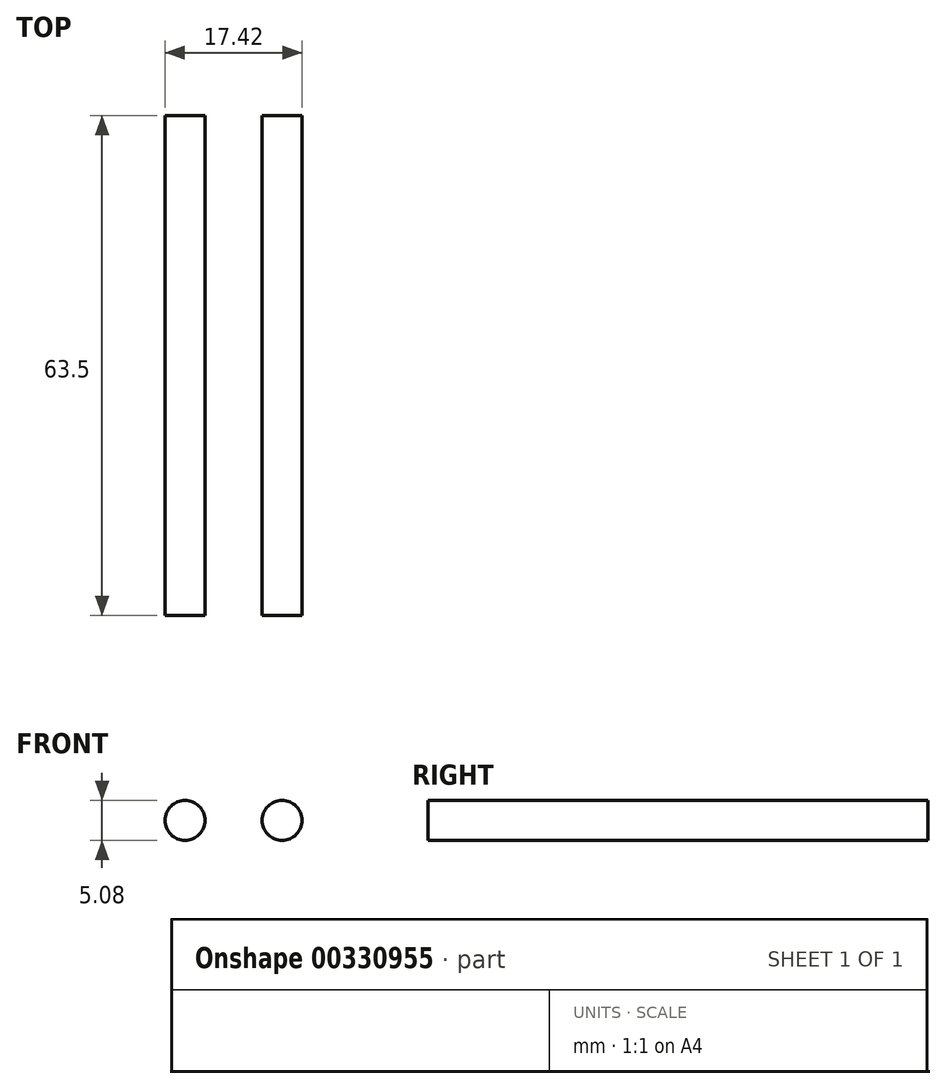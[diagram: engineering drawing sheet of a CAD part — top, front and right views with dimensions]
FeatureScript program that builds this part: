
annotation { "Feature Type Name" : "Feature", "Feature Type Description" : "" }
export const myFeature = defineFeature(function(context is Context, id is Id, definition is map)
    precondition{}
    {
        {
            var Q0;
            Q0=qCreatedBy(makeId("Front.planeOp"),FACE);
            var sketch = newSketch(context, id + "F0", { "sketchPlane" : qUnion([Q0])});
            skLineSegment(sketch, "E0", {"start": v(-3.56, 30.72) * mm, "end": v(-30.55, -10.44) * mm});
            skLineSegment(sketch, "E1", {"start": v(-25.24, -20.27) * mm, "end": v(0, -20.27) * mm});
            skLineSegment(sketch, "E2.MirrorCS", {"start": v(3.56, 30.72) * mm, "end": v(30.55, -10.44) * mm});
            skLineSegment(sketch, "E3.MirrorCS", {"start": v(25.24, -20.27) * mm, "end": v(0, -20.27) * mm});
            skPoint(sketch, "E4.visualSharp", {"position": v(-37, -20.27) * mm});
            skArc(sketch, "E4.filletArc", {"start": v(-30.55, -10.44) * mm, "mid": v(-30.83, -16.94) * mm, "end": v(-25.24, -20.27) * mm});
            skPoint(sketch, "E5.visualSharp", {"position": v(37, -20.27) * mm});
            skArc(sketch, "E5.filletArc", {"start": v(25.24, -20.27) * mm, "mid": v(30.83, -16.94) * mm, "end": v(30.55, -10.44) * mm});
            skArc(sketch, "E6", {"start": v(3.56, 30.72) * mm, "mid": v(6.9, 35.56) * mm, "end": v(7.88, 29.76) * mm});
            skArc(sketch, "E7.MirrorCS", {"start": v(-3.56, 30.72) * mm, "mid": v(-6.9, 35.56) * mm, "end": v(-7.88, 29.76) * mm});
            skSolve(sketch);
        }
        {
            var Q0;
            Q0=qSketchRegion(id+"F0",true);
            var Q1;
            Q1=sQuery(id+"F0.wireOp",EDGE,"E6");
            var Q2;
            Q2=sQuery(id+"F0.wireOp",EDGE,"E7.MirrorCS");
            var Q3;
            Q3=sQuery(id+"F0.wireOp",EDGE,"E4.filletArc");
            var Q4;
            Q4=sQuery(id+"F0.wireOp",EDGE,"E1");
            var Q5;
            Q5=sQuery(id+"F0.wireOp",EDGE,"E3.MirrorCS");
            var Q6;
            Q6=sQuery(id+"F0.wireOp",EDGE,"E5.filletArc");
            var Q7;
            Q7=sQuery(id+"F0.wireOp",EDGE,"E0");
            var Q8;
            Q8=sQuery(id+"F0.wireOp",EDGE,"E2.MirrorCS");
            extrude(context, id + "F1", {"entities" : qUnion([Q0]), "bodyType" : ToolBodyType.SURFACE, "surfaceEntities" : qUnion([Q1, Q2, Q3, Q4, Q5, Q6, Q7, Q8]), "depth" : 31.75 * mm, "hasDraft" : true, "draftAngle" : 3 * degree, "hasSecondDirection" : true, "secondDirectionOppositeDirection" : true, "secondDirectionDepth" : 31.75 * mm});
        }
        {
            var Q0;
            Q0=qCreatedBy(makeId("Top.planeOp"),FACE);
            cPlane(context, id + "F2", {"entities" : qUnion([Q0]), "cplaneType" : CPlaneType.OFFSET, "offset" : 30.72 * mm, "width" : 152.4 * mm, "height" : 152.4 * mm});
        }
        {
            var Q0;
            Q0=qCreatedBy(makeId("Front.planeOp"),FACE);
            var sketch = newSketch(context, id + "F3", { "sketchPlane" : qUnion([Q0])});
            skCircle(sketch, "E8", {"center": v(6.17, 32.41) * mm, "radius": 2.54 * mm});
            skCircle(sketch, "E9.MirrorC", {"center": v(-6.17, 32.41) * mm, "radius": 2.54 * mm});
            skSolve(sketch);
        }
        {
            var Q0;
            Q0 = qSketchRegion(id + "F3", true);
            extrude(context, id + "F4", {"entities" : qUnion([Q0]), "endBound" : BoundingType.SYMMETRIC, "depth" : 63.5 * mm});
        }
    });
